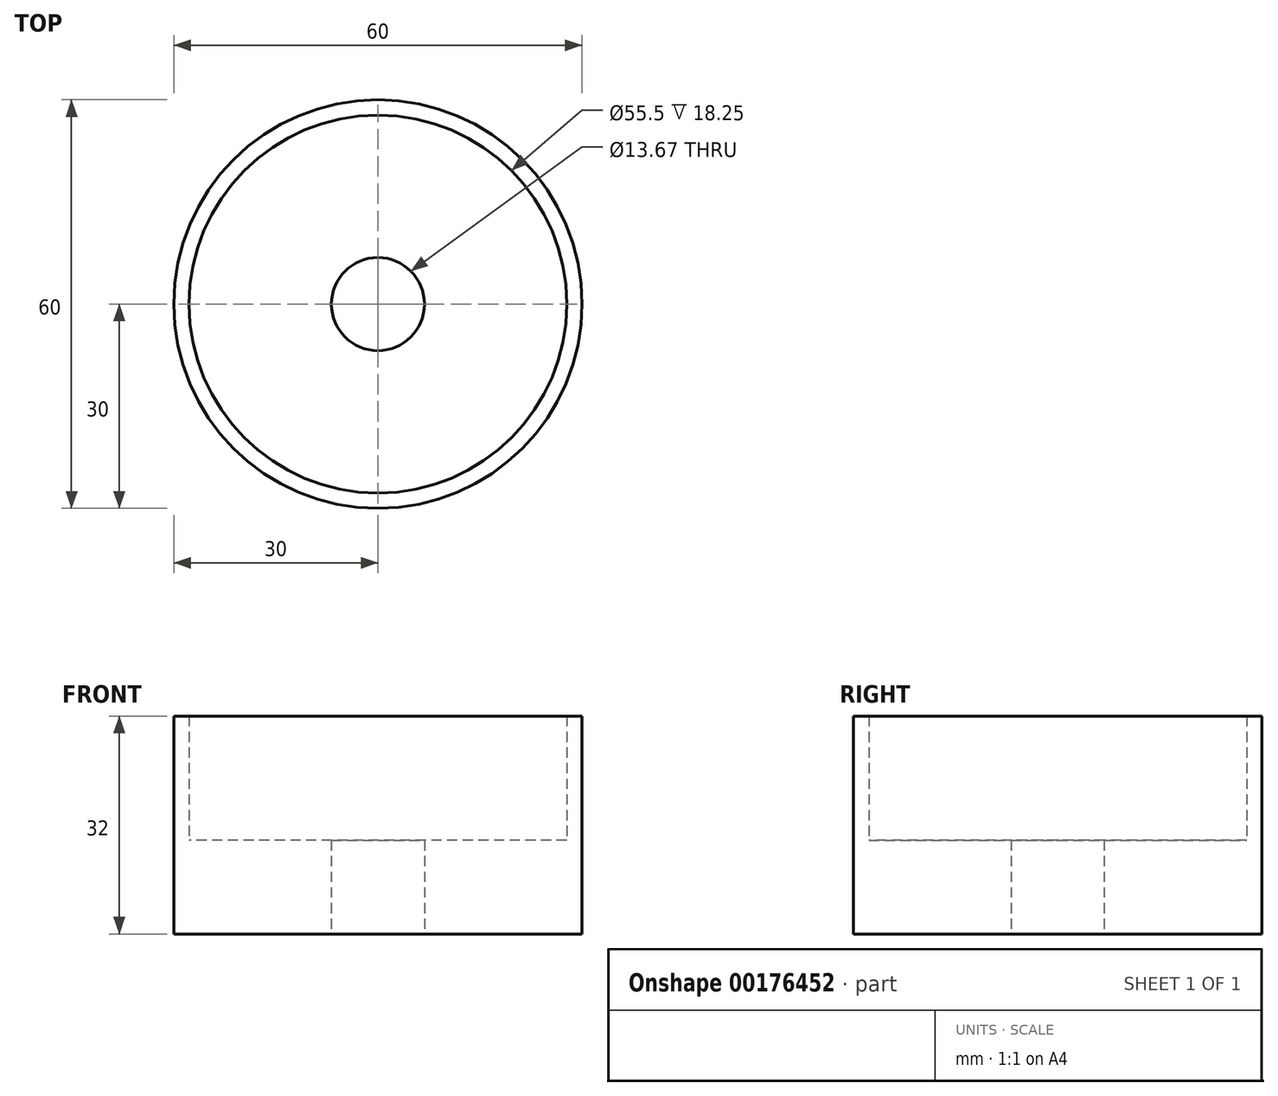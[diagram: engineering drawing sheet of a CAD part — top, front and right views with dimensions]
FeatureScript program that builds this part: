
annotation { "Feature Type Name" : "Feature", "Feature Type Description" : "" }
export const myFeature = defineFeature(function(context is Context, id is Id, definition is map)
    precondition{}
    {
        {
            var Q0;
            Q0=qCreatedBy(makeId("Top.planeOp"),FACE);
            var sketch = newSketch(context, id + "F0", { "sketchPlane" : qUnion([Q0])});
            skCircle(sketch, "E0", {"center": v(0, 0) * mm, "radius": 30 * mm});
            skSolve(sketch);
        }
        {
            var Q0;
            Q0=makeQuery(id+"F0.imprint","IMPRINT",FACE,{"disambiguationData":[TD([[makeQuery(id+"F0.imprint","IMPRINT",EDGE,{"derivedFrom":sQuery(id+"F0.wireOp",EDGE,"E0")}),1.0]])]});
            extrude(context, id + "F1", {"entities" : qUnion([Q0]), "depth" : 13.75 * mm});
        }
        {
            var Q0;
            Q0=makeQuery(id+"F1.opExtrude","CAP_FACE",FACE,{"disambiguationData":[OSD([sQuery(id+"F0.wireOp",EDGE,"E0")])],"isStart":false});
            var sketch = newSketch(context, id + "F2", { "sketchPlane" : qUnion([Q0])});
            skCircle(sketch, "E1", {"center": v(0, 0) * mm, "radius": 27.75 * mm});
            skSolve(sketch);
        }
        {
            var Q0;
            Q0=makeQuery(id+"F2.imprint","IMPRINT",FACE,{"disambiguationData":[TD([[makeQuery(id+"F2.imprint","IMPRINT",EDGE,{"derivedFrom":sQuery(id+"F2.wireOp",EDGE,"E1")}),-1.0]])]});
            extrude(context, id + "F3", {"entities" : qUnion([Q0]), "operationType" : NewBodyOperationType.ADD, "depth" : 18.25 * mm});
        }
        {
            var Q0;
            Q0=makeQuery(id+"F1.opExtrude","CAP_FACE",FACE,{"disambiguationData":[OSD([sQuery(id+"F0.wireOp",EDGE,"E0")])],"isStart":true});
            var sketch = newSketch(context, id + "F4", { "sketchPlane" : qUnion([Q0])});
            skCircle(sketch, "E2", {"center": v(0, 0) * mm, "radius": 6.83 * mm});
            skSolve(sketch);
        }
        {
            var Q0;
            Q0=sQuery(id+"F4.wireOp",VERTEX,"E2.center");
            var Q1;
            Q1=makeQuery(id+"F1.opExtrude","SWEPT_BODY",BODY,{"disambiguationData":[OSD([sQuery(id+"F0.wireOp",EDGE,"E0")])]});
            hole(context, id + "F5", {"style" : HoleStyle.SIMPLE, "endStyle" : HoleEndStyle.BLIND, "holeDiameter" : 13.67 * mm, "holeDepth" : 13.75 * mm, "startFromSketch" : true, "locations" : qUnion([Q0]), "scope" : qUnion([Q1])});
        }
    });
